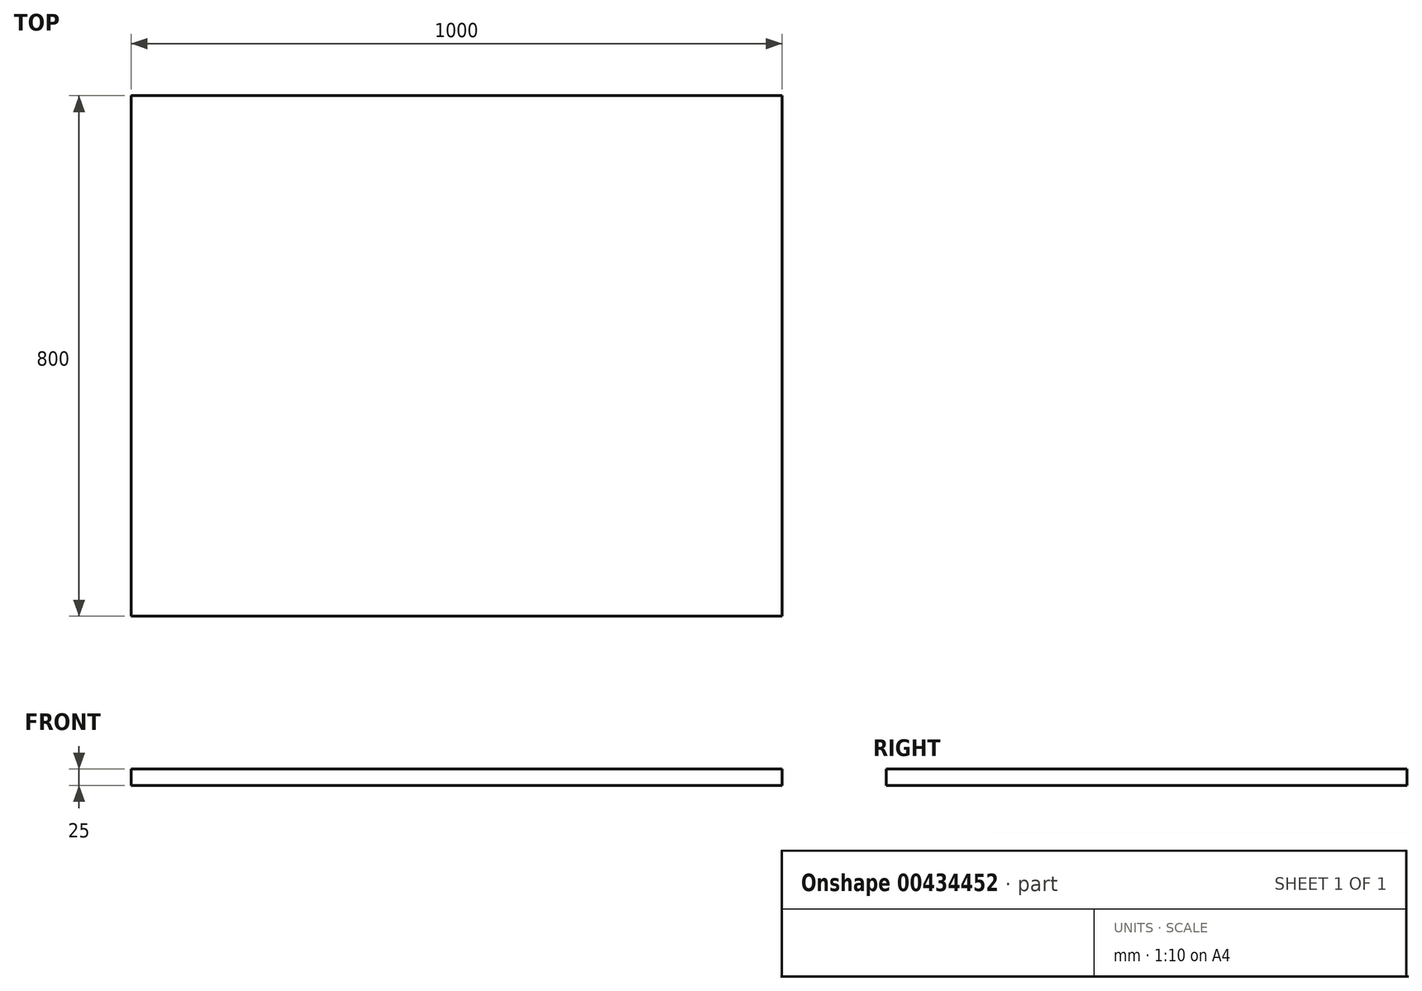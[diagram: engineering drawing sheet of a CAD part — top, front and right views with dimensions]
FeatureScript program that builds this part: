
annotation { "Feature Type Name" : "Feature", "Feature Type Description" : "" }
export const myFeature = defineFeature(function(context is Context, id is Id, definition is map)
    precondition{}
    {
        {
            var Q0;
            Q0=qCreatedBy(makeId("Top.planeOp"),FACE);
            var sketch = newSketch(context, id + "F0", { "sketchPlane" : qUnion([Q0])});
            skLineSegment(sketch, "E0.bottom", {"start": v(-352.46, 403.26) * mm, "end": v(647.54, 403.26) * mm});
            skLineSegment(sketch, "E0.top", {"start": v(-352.46, -396.74) * mm, "end": v(647.54, -396.74) * mm});
            skLineSegment(sketch, "E0.left", {"start": v(-352.46, 403.26) * mm, "end": v(-352.46, -396.74) * mm});
            skLineSegment(sketch, "E0.right", {"start": v(647.54, 403.26) * mm, "end": v(647.54, -396.74) * mm});
            skSolve(sketch);
        }
        {
            var Q0;
            Q0=makeQuery(id+"F0.imprint","IMPRINT",FACE,{"disambiguationData":[TD([[makeQuery(id+"F0.imprint","IMPRINT",EDGE,{"derivedFrom":sQuery(id+"F0.wireOp",EDGE,"E0.bottom")}),-1.0]])]});
            extrude(context, id + "F1", {"entities" : qUnion([Q0]), "depth" : 25 * mm, "offsetDistance" : 25 * mm});
        }
    });
